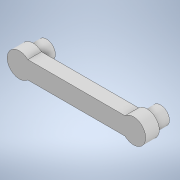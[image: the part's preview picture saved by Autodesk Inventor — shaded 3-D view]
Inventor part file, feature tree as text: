
AUTODESK INVENTOR PART (.ipt)
format: ipt  version: 2022 (Build 260153000, 153)  size: 120,832 bytes
history: native  units: in
note: dims shown in document units (in); Inventor stores cm internally (conversion verified against a paired STEP export)
features: extrude x2, sketch x1
ambient origin geometry x8: Origin, YZ Plane, XZ Plane, XY Plane, X Axis, Y Axis, Z Axis, Center Point
bodies: Body1 (feature_tree)
feature tree (3):
  sketch  "Sketch2"  dims[d0=0.1969in d1=0.0in d2=0.1969in d3=0.0in d4=0.2559in d6=0.3543in d7=0.2559in d8=1.6535in]
  extrude  "Extrusion1"  Depth=0.1969in TaperAngle=0.0deg
  extrude  "Extrusion2"  Depth=0.2559in
